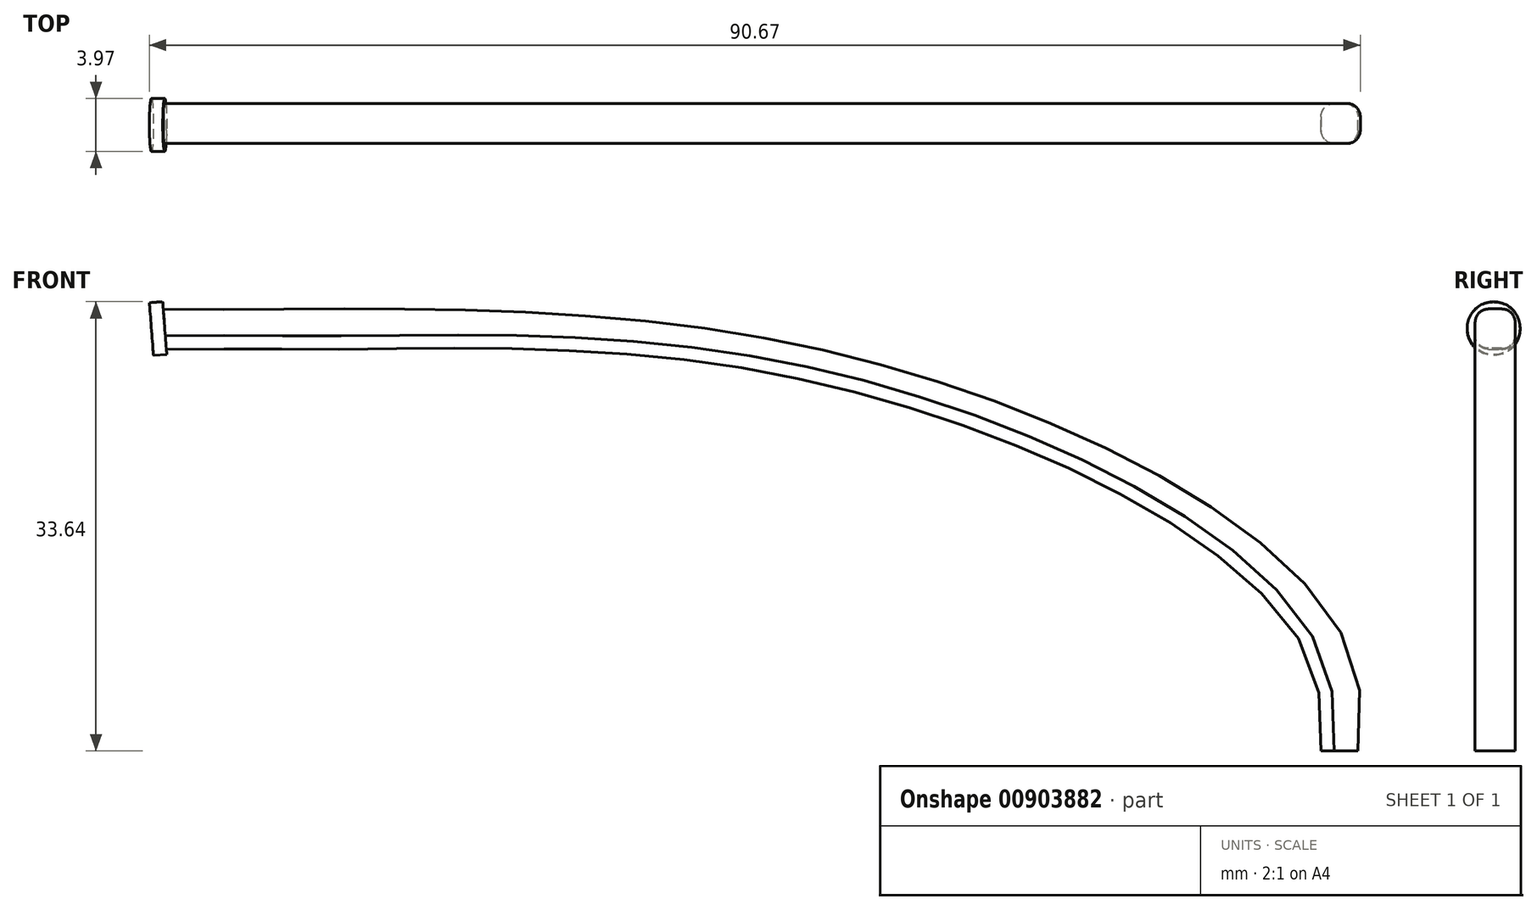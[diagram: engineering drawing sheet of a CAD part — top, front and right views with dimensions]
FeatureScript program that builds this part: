
annotation { "Feature Type Name" : "Feature", "Feature Type Description" : "" }
export const myFeature = defineFeature(function(context is Context, id is Id, definition is map)
    precondition{}
    {
        {
            var Q0;
            Q0=qCreatedBy(makeId("Front.planeOp"),FACE);
            var sketch = newSketch(context, id + "F0", { "sketchPlane" : qUnion([Q0])});
            skFitSpline(sketch, "E0", {"points": [v(-60.13, 26.67) * mm, v(-15.52, 24.6) * mm, v(19.89, 10.8) * mm, v(29.09, 0) * mm, v(29.32, -6.4) * mm], "startDerivative": vector(121.84, -0.73) * mm, "endDerivative": vector(-3.11, -42.77) * mm});
            skFitSpline(sketch, "E1", {"points": [v(-59.9, 23.68) * mm, v(-46.56, 23.68) * mm, v(-16.9, 22.3) * mm, v(15.06, 10.8) * mm, v(25.87, 0) * mm, v(26.56, -6.4) * mm], "startDerivative": vector(73.26, 1.17) * mm, "endDerivative": vector(0.88, -46.93) * mm});
            skLineSegment(sketch, "E2", {"start": v(-60.13, 26.67) * mm, "end": v(-59.9, 23.68) * mm});
            skLineSegment(sketch, "E3", {"start": v(29.32, -6.4) * mm, "end": v(26.56, -6.4) * mm});
            skSolve(sketch);
        }
        {
            var Q0;
            Q0 = qSketchRegion(id + "F0", true);
            extrude(context, id + "F1", {"entities" : qUnion([Q0]), "depth" : 3 * mm, "offsetDistance" : 25 * mm});
        }
        {
            var Q0;
            Q0=makeQuery(id+"F1.opExtrude","CAP_EDGE",EDGE,{"disambiguationData":[OSD([sQuery(id+"F0.wireOp",EDGE,"E0")])],"isStart":false});
            var Q1;
            Q1=makeQuery(id+"F1.opExtrude","CAP_EDGE",EDGE,{"disambiguationData":[OSD([sQuery(id+"F0.wireOp",EDGE,"E0")])],"isStart":true});
            var Q2;
            Q2=makeQuery(id+"F1.opExtrude","CAP_EDGE",EDGE,{"disambiguationData":[OSD([sQuery(id+"F0.wireOp",EDGE,"E1")])],"isStart":true});
            var Q3;
            Q3=makeQuery(id+"F1.opExtrude","CAP_EDGE",EDGE,{"disambiguationData":[OSD([sQuery(id+"F0.wireOp",EDGE,"E1")])],"isStart":false});
            fillet(context, id + "F2", {"entities" : qUnion([Q0, Q1, Q2, Q3]), "radius" : 1 * mm, "tangentPropagation" : true, "allowEdgeOverflow" : false});
        }
        {
            var Q0;
            Q0=makeQuery(id+"F1.opExtrude","SWEPT_FACE",FACE,{"disambiguationData":[OSD([sQuery(id+"F0.wireOp",EDGE,"E2")])]});
            var sketch = newSketch(context, id + "F3", { "sketchPlane" : qUnion([Q0])});
            skCircle(sketch, "E4", {"center": v(1.61, 29.8) * mm, "radius": 1.98 * mm});
            skSolve(sketch);
        }
        {
            var Q0;
            Q0 = qSketchRegion(id + "F3", true);
            extrude(context, id + "F4", {"entities" : qUnion([Q0]), "operationType" : NewBodyOperationType.ADD, "depth" : 1 * mm, "offsetDistance" : 25 * mm});
        }
    });
